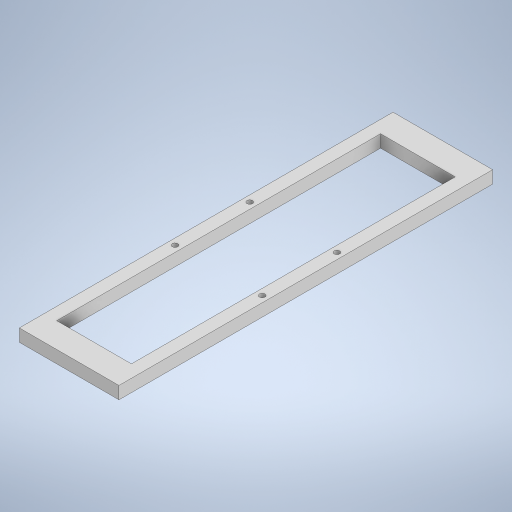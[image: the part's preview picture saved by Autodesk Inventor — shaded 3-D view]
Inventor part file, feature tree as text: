
AUTODESK INVENTOR PART (.ipt)
format: ipt  version: 2024 (Build 280153000, 153)  size: 254,976 bytes
history: native  units: mm
features: other x1, extrude x1, sketch x1
ambient origin geometry x8: Origin, YZ Plane, XZ Plane, XY Plane, X Axis, Y Axis, Z Axis, Center Point
bodies: Body1 (feature_tree)
feature tree (3):
  other  "솔리드1"
  extrude  "돌출1"  Depth=80.0mm
  sketch  "스케치1"
